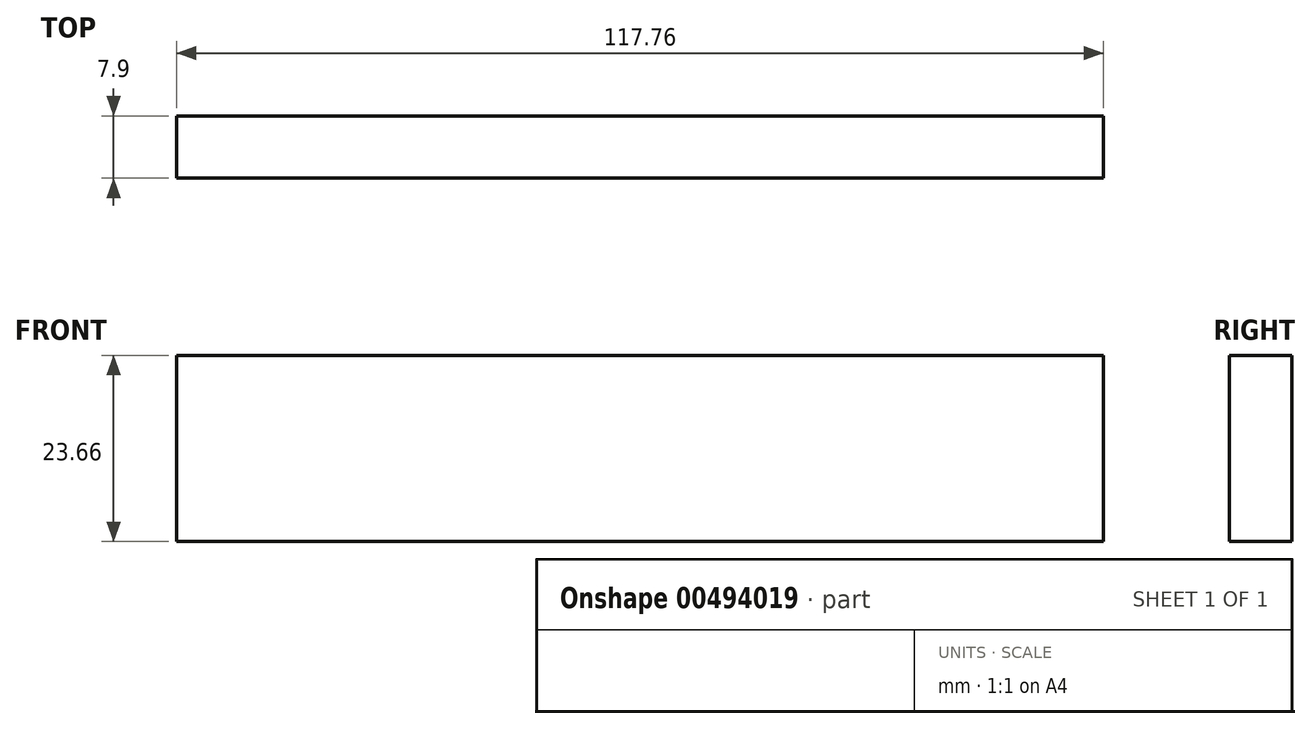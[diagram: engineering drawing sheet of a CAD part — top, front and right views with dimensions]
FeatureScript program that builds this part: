
annotation { "Feature Type Name" : "Feature", "Feature Type Description" : "" }
export const myFeature = defineFeature(function(context is Context, id is Id, definition is map)
    precondition{}
    {
        {
            var Q0;
            Q0=qCreatedBy(makeId("Front.planeOp"),FACE);
            var sketch = newSketch(context, id + "F0", { "sketchPlane" : qUnion([Q0])});
            skLineSegment(sketch, "E0.bottom", {"start": v(-58.88, 11.83) * mm, "end": v(58.88, 11.83) * mm});
            skLineSegment(sketch, "E0.top", {"start": v(-58.88, -11.83) * mm, "end": v(58.88, -11.83) * mm});
            skLineSegment(sketch, "E0.left", {"start": v(-58.88, 11.83) * mm, "end": v(-58.88, -11.83) * mm});
            skLineSegment(sketch, "E0.right", {"start": v(58.88, 11.83) * mm, "end": v(58.88, -11.83) * mm});
            skPoint(sketch, "E0.middle", {"position": v(0, 0) * mm});
            skSolve(sketch);
        }
        {
            var Q0;
            Q0=makeQuery(id+"F0.imprint","IMPRINT",FACE,{"disambiguationData":[TD([[makeQuery(id+"F0.imprint","IMPRINT",EDGE,{"derivedFrom":sQuery(id+"F0.wireOp",EDGE,"E0.bottom")}),-1.0]])]});
            extrude(context, id + "F1", {"entities" : qUnion([Q0]), "depth" : 7.9 * mm});
        }
    });
